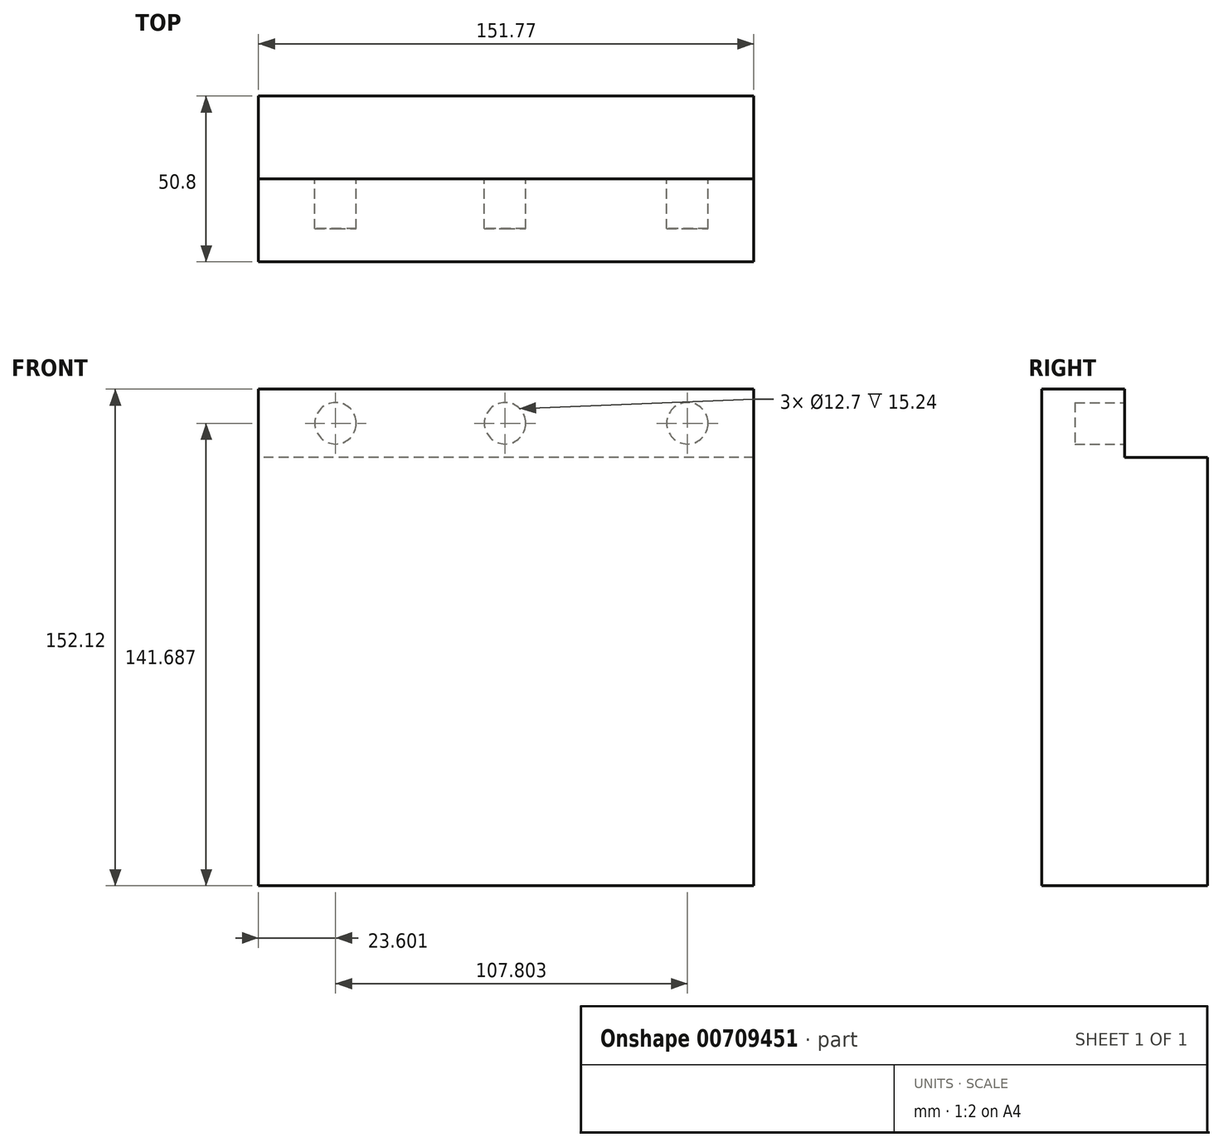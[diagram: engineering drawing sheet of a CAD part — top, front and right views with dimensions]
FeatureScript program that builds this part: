
annotation { "Feature Type Name" : "Feature", "Feature Type Description" : "" }
export const myFeature = defineFeature(function(context is Context, id is Id, definition is map)
    precondition{}
    {
        {
            var Q0;
            Q0=qCreatedBy(makeId("Front.planeOp"),FACE);
            var sketch = newSketch(context, id + "F0", { "sketchPlane" : qUnion([Q0])});
            skLineSegment(sketch, "E0", {"start": v(-75.53, 61.94) * mm, "end": v(-75.53, -75.8) * mm});
            skLineSegment(sketch, "E1", {"start": v(76.24, -75.8) * mm, "end": v(76.24, 76.33) * mm});
            skLineSegment(sketch, "E2", {"start": v(76.24, 76.33) * mm, "end": v(-75.53, 76.33) * mm});
            skLineSegment(sketch, "E3", {"start": v(-75.53, 76.33) * mm, "end": v(-75.53, 61.94) * mm});
            skLineSegment(sketch, "E4", {"start": v(-75.53, -75.8) * mm, "end": v(72.82, -75.8) * mm});
            skLineSegment(sketch, "E5", {"start": v(76.24, -75.8) * mm, "end": v(72.82, -75.8) * mm});
            skSolve(sketch);
        }
        {
            var Q0;
            Q0=makeQuery(id+"F0.imprint","IMPRINT",FACE,{"disambiguationData":[TD([[makeQuery(id+"F0.imprint","IMPRINT",EDGE,{"derivedFrom":sQuery(id+"F0.wireOp",EDGE,"E0")}),1.0]])]});
            extrude(context, id + "F1", {"entities" : qUnion([Q0]), "depth" : 25.4 * mm, "offsetDistance" : 25.4 * mm});
        }
        {
            var Q0;
            Q0=makeQuery(id+"F1.opExtrude","CAP_FACE",FACE,{"disambiguationData":[OSD([sQuery(id+"F0.wireOp",EDGE,"E0"),sQuery(id+"F0.wireOp",EDGE,"E1"),sQuery(id+"F0.wireOp",EDGE,"E2"),sQuery(id+"F0.wireOp",EDGE,"E3"),sQuery(id+"F0.wireOp",EDGE,"E4"),sQuery(id+"F0.wireOp",EDGE,"E5")])],"isStart":true});
            var sketch = newSketch(context, id + "F2", { "sketchPlane" : qUnion([Q0])});
            skLineSegment(sketch, "E6.bottom", {"start": v(-76.24, 55.47) * mm, "end": v(75.53, 55.47) * mm});
            skLineSegment(sketch, "E6.top", {"start": v(-76.24, -75.8) * mm, "end": v(75.53, -75.8) * mm});
            skLineSegment(sketch, "E6.left", {"start": v(-76.24, 55.47) * mm, "end": v(-76.24, -75.8) * mm});
            skLineSegment(sketch, "E6.right", {"start": v(75.53, 55.47) * mm, "end": v(75.53, -75.8) * mm});
            skSolve(sketch);
        }
        {
            var Q0;
            Q0 = qSketchRegion(id + "F2", true);
            extrude(context, id + "F3", {"entities" : qUnion([Q0]), "operationType" : NewBodyOperationType.ADD, "depth" : 25.4 * mm, "offsetDistance" : 25.4 * mm});
        }
        {
            var Q0;
            Q0=makeQuery(id+"F1.opExtrude","CAP_FACE",FACE,{"disambiguationData":[OSD([sQuery(id+"F0.wireOp",EDGE,"E0"),sQuery(id+"F0.wireOp",EDGE,"E1"),sQuery(id+"F0.wireOp",EDGE,"E2"),sQuery(id+"F0.wireOp",EDGE,"E3"),sQuery(id+"F0.wireOp",EDGE,"E4"),sQuery(id+"F0.wireOp",EDGE,"E5")])],"isStart":true});
            var sketch = newSketch(context, id + "F4", { "sketchPlane" : qUnion([Q0])});
            skCircle(sketch, "E7", {"center": v(-55.87, 65.9) * mm, "radius": 6.35 * mm});
            skPoint(sketch, "E7.centerSnap0", {"position": v(-76.24, 65.9) * mm});
            skCircle(sketch, "E8", {"center": v(0, 65.9) * mm, "radius": 6.35 * mm});
            skCircle(sketch, "E9", {"center": v(51.93, 65.9) * mm, "radius": 6.35 * mm});
            skSolve(sketch);
        }
        {
            var Q0;
            Q0=makeQuery(id+"F4.imprint","IMPRINT",FACE,{"disambiguationData":[TD([[makeQuery(id+"F4.imprint","IMPRINT",EDGE,{"derivedFrom":sQuery(id+"F4.wireOp",EDGE,"E7")}),1.0]])]});
            var Q1;
            Q1=makeQuery(id+"F4.imprint","IMPRINT",FACE,{"disambiguationData":[TD([[makeQuery(id+"F4.imprint","IMPRINT",EDGE,{"derivedFrom":sQuery(id+"F4.wireOp",EDGE,"E8")}),1.0]])]});
            var Q2;
            Q2=makeQuery(id+"F4.imprint","IMPRINT",FACE,{"disambiguationData":[TD([[makeQuery(id+"F4.imprint","IMPRINT",EDGE,{"derivedFrom":sQuery(id+"F4.wireOp",EDGE,"E9")}),1.0]])]});
            extrude(context, id + "F5", {"entities" : qUnion([Q0, Q1, Q2]), "operationType" : NewBodyOperationType.REMOVE, "oppositeDirection" : true, "depth" : 15.24 * mm, "offsetDistance" : 25.4 * mm});
        }
    });
